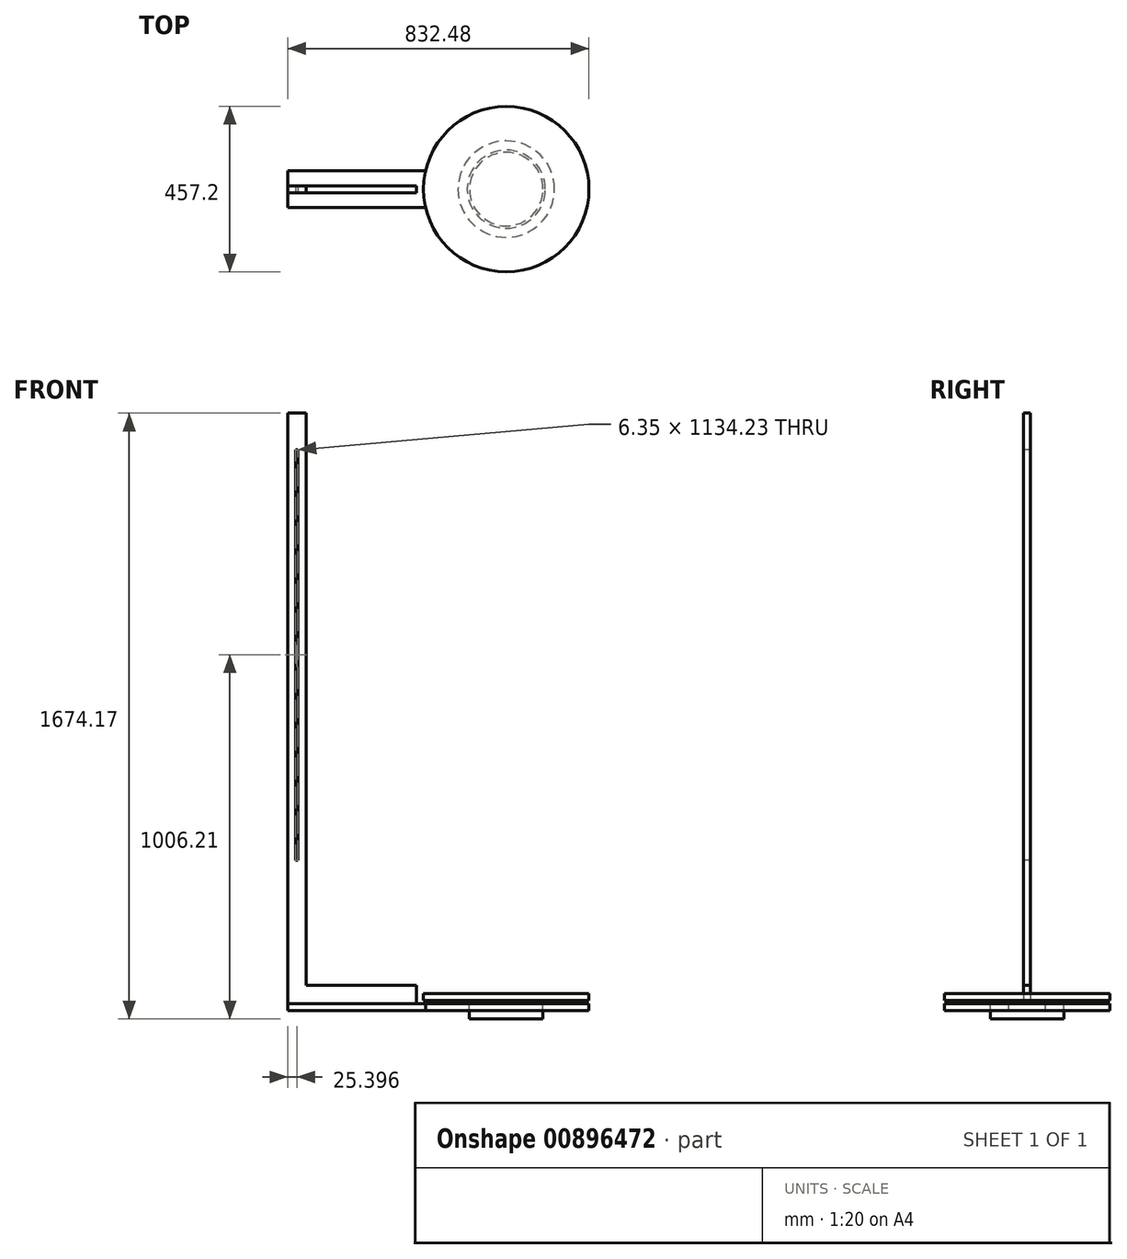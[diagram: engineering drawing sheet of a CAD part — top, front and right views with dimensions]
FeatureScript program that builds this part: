
annotation { "Feature Type Name" : "Feature", "Feature Type Description" : "" }
export const myFeature = defineFeature(function(context is Context, id is Id, definition is map)
    precondition{}
    {
        {
            var Q0;
            Q0=qCreatedBy(makeId("Top.planeOp"),FACE);
            var sketch = newSketch(context, id + "F0", { "sketchPlane" : qUnion([Q0])});
            skCircle(sketch, "E0", {"center": v(0, 0) * mm, "radius": 228.6 * mm});
            skSolve(sketch);
        }
        {
            var Q0;
            Q0=makeQuery(id+"F0.imprint","IMPRINT",FACE,{"disambiguationData":[TD([[makeQuery(id+"F0.imprint","IMPRINT",EDGE,{"derivedFrom":sQuery(id+"F0.wireOp",EDGE,"E0")}),1.0]])]});
            extrude(context, id + "F1", {"entities" : qUnion([Q0]), "depth" : 19.05 * mm, "offsetDistance" : 25.4 * mm});
        }
        {
            var Q0;
            Q0=makeQuery(id+"F1.opExtrude","CAP_FACE",FACE,{"disambiguationData":[OSD([sQuery(id+"F0.wireOp",EDGE,"E0")])],"isStart":true});
            var sketch = newSketch(context, id + "F2", { "sketchPlane" : qUnion([Q0])});
            skCircle(sketch, "E1", {"center": v(0, 0) * mm, "radius": 101.6 * mm});
            skSolve(sketch);
        }
        {
            var Q0;
            Q0 = qSketchRegion(id + "F2", true);
            var Q1;
            Q1=makeQuery(id+"F2.imprint","IMPRINT",FACE,{"disambiguationData":[TD([[makeQuery(id+"F2.imprint","IMPRINT",EDGE,{"derivedFrom":sQuery(id+"F2.wireOp",EDGE,"E1")}),1.0]])]});
            extrude(context, id + "F3", {"entities" : qUnion([Q0, Q1]), "depth" : 50.8 * mm, "offsetDistance" : 25.4 * mm});
        }
        {
            var Q0;
            Q0=makeQuery(id+"F1.opExtrude","CAP_FACE",FACE,{"disambiguationData":[OSD([sQuery(id+"F0.wireOp",EDGE,"E0")])],"isStart":true});
            var sketch = newSketch(context, id + "F4", { "sketchPlane" : qUnion([Q0])});
            skCircle(sketch, "E2", {"center": v(0, 0) * mm, "radius": 107.95 * mm});
            skCircle(sketch, "E3", {"center": v(0, 0) * mm, "radius": 133.35 * mm});
            skSolve(sketch);
        }
        {
            var Q0;
            Q0 = qSketchRegion(id + "F4", true);
            extrude(context, id + "F5", {"entities" : qUnion([Q0]), "depth" : 8.38 * mm, "offsetDistance" : 25.4 * mm});
        }
        {
            var Q0;
            Q0=makeQuery(id+"F5.opExtrude","CAP_FACE",FACE,{"disambiguationData":[OSD([sQuery(id+"F4.wireOp",EDGE,"E2"),sQuery(id+"F4.wireOp",EDGE,"E3")])],"isStart":false});
            var sketch = newSketch(context, id + "F6", { "sketchPlane" : qUnion([Q0])});
            skLineSegment(sketch, "E4", {"start": v(-431.45, 0) * mm, "end": v(-431.45, 50.8) * mm, "construction": true});
            skLineSegment(sketch, "E5", {"start": v(-431.45, 0) * mm, "end": v(-431.45, -50.8) * mm, "construction": true});
            skArc(sketch, "E6", {"start": v(-222.88, -50.8) * mm, "mid": v(228.6, 0) * mm, "end": v(-222.88, 50.8) * mm});
            skLineSegment(sketch, "E7", {"start": v(-222.88, 50.8) * mm, "end": v(-603.88, 50.8) * mm});
            skLineSegment(sketch, "E8", {"start": v(-603.88, 50.8) * mm, "end": v(-603.88, -50.8) * mm});
            skLineSegment(sketch, "E9", {"start": v(-603.88, -50.8) * mm, "end": v(-222.88, -50.8) * mm});
            skLineSegment(sketch, "E10", {"start": v(0, 0) * mm, "end": v(-605.21, 0) * mm, "construction": true});
            skPoint(sketch, "E10.endSnap0", {"position": v(-603.88, 0) * mm});
            skSolve(sketch);
        }
        {
            var Q0;
            Q0 = qSketchRegion(id + "F6", true);
            extrude(context, id + "F7", {"entities" : qUnion([Q0]), "depth" : 19.05 * mm, "offsetDistance" : 25.4 * mm});
        }
        {
            var Q0;
            Q0=makeQuery(id+"F7.opExtrude","CAP_FACE",FACE,{"disambiguationData":[OSD([sQuery(id+"F6.wireOp",EDGE,"E6"),sQuery(id+"F6.wireOp",EDGE,"E7"),sQuery(id+"F6.wireOp",EDGE,"E8"),sQuery(id+"F6.wireOp",EDGE,"E9")])],"isStart":true});
            var sketch = newSketch(context, id + "F8", { "sketchPlane" : qUnion([Q0])});
            skLineSegment(sketch, "E11", {"start": v(-299.08, 9.52) * mm, "end": v(-248.28, 9.52) * mm});
            skLineSegment(sketch, "E12", {"start": v(-248.28, 9.52) * mm, "end": v(-248.28, -9.53) * mm});
            skLineSegment(sketch, "E13", {"start": v(-248.28, -9.53) * mm, "end": v(-299.08, -9.53) * mm});
            skLineSegment(sketch, "E14", {"start": v(-299.08, -9.53) * mm, "end": v(-299.08, 9.52) * mm});
            skSolve(sketch);
        }
        {
            var Q0;
            Q0=makeQuery(id+"F8.imprint","IMPRINT",FACE,{"disambiguationData":[TD([[makeQuery(id+"F8.imprint","IMPRINT",EDGE,{"derivedFrom":sQuery(id+"F8.wireOp",EDGE,"E11")}),-1.0]])]});
            extrude(context, id + "F9", {"entities" : qUnion([Q0]), "depth" : 50.8 * mm, "offsetDistance" : 25.4 * mm});
        }
        {
            var Q0;
            Q0=makeQuery(id+"F9.opExtrude","SWEPT_FACE",FACE,{"disambiguationData":[OSD([sQuery(id+"F8.wireOp",EDGE,"E13")])]});
            var sketch = newSketch(context, id + "F10", { "sketchPlane" : qUnion([Q0])});
            skLineSegment(sketch, "E15", {"start": v(-245, 17.02) * mm, "end": v(-245, 1541.02) * mm, "construction": true});
            skPoint(sketch, "E15.startSnap0", {"position": v(-248.28, 17.02) * mm});
            skLineSegment(sketch, "E16", {"start": v(-299.08, -8.38) * mm, "end": v(-603.88, -8.38) * mm});
            skLineSegment(sketch, "E17", {"start": v(-603.88, -8.38) * mm, "end": v(-603.88, 1623.37) * mm});
            skLineSegment(sketch, "E18", {"start": v(-603.88, 1623.37) * mm, "end": v(-553.08, 1623.37) * mm});
            skLineSegment(sketch, "E19", {"start": v(-553.08, 1623.37) * mm, "end": v(-553.08, 42.42) * mm});
            skLineSegment(sketch, "E20", {"start": v(-553.08, 42.42) * mm, "end": v(-299.08, 42.42) * mm});
            skSolve(sketch);
        }
        {
            var Q0;
            Q0=makeQuery(id+"F10.imprint","IMPRINT",FACE,{"disambiguationData":[TD([[makeQuery(id+"F10.imprint","IMPRINT",EDGE,{"derivedFrom":sQuery(id+"F10.wireOp",EDGE,"E16")}),-1.0]])]});
            extrude(context, id + "F11", {"entities" : qUnion([Q0]), "operationType" : NewBodyOperationType.ADD, "oppositeDirection" : true, "depth" : 19.05 * mm, "offsetDistance" : 25.4 * mm});
        }
        {
            var Q0;
            {var subQ0=sQuery(id+"F8.wireOp",EDGE,"E13");Q0=makeQuery(id+"F11.boolean.opBoolean","MERGE",FACE,{"derivedFrom":[makeQuery(id+"F9.opExtrude","SWEPT_FACE",FACE,{"disambiguationData":[OSD([subQ0])]}),makeQuery(id+"F11.opExtrude","CAP_FACE",FACE,{"disambiguationData":[OSD([sQuery(id+"F6.wireOp",EDGE,"E8"),subQ0,sQuery(id+"F8.wireOp",EDGE,"E14"),sQuery(id+"F10.wireOp",EDGE,"E16"),sQuery(id+"F10.wireOp",EDGE,"E17"),sQuery(id+"F10.wireOp",EDGE,"E18"),sQuery(id+"F10.wireOp",EDGE,"E19"),sQuery(id+"F10.wireOp",EDGE,"E20")])],"isStart":true})]});}
            var sketch = newSketch(context, id + "F12", { "sketchPlane" : qUnion([Q0])});
            skLineSegment(sketch, "E21.bottom", {"start": v(-581.66, 1522.52) * mm, "end": v(-575.3, 1522.52) * mm});
            skLineSegment(sketch, "E21.top", {"start": v(-581.66, 388.3) * mm, "end": v(-575.3, 388.3) * mm});
            skLineSegment(sketch, "E21.left", {"start": v(-581.66, 1522.52) * mm, "end": v(-581.66, 388.3) * mm});
            skLineSegment(sketch, "E21.right", {"start": v(-575.3, 1522.52) * mm, "end": v(-575.3, 388.3) * mm});
            skSolve(sketch);
        }
        {
            var Q0;
            Q0 = qSketchRegion(id + "F12", true);
            extrude(context, id + "F13", {"entities" : qUnion([Q0]), "operationType" : NewBodyOperationType.REMOVE, "endBound" : BoundingType.UP_TO_NEXT, "oppositeDirection" : true, "depth" : 25.4 * mm, "offsetDistance" : 25.4 * mm});
        }
    });
